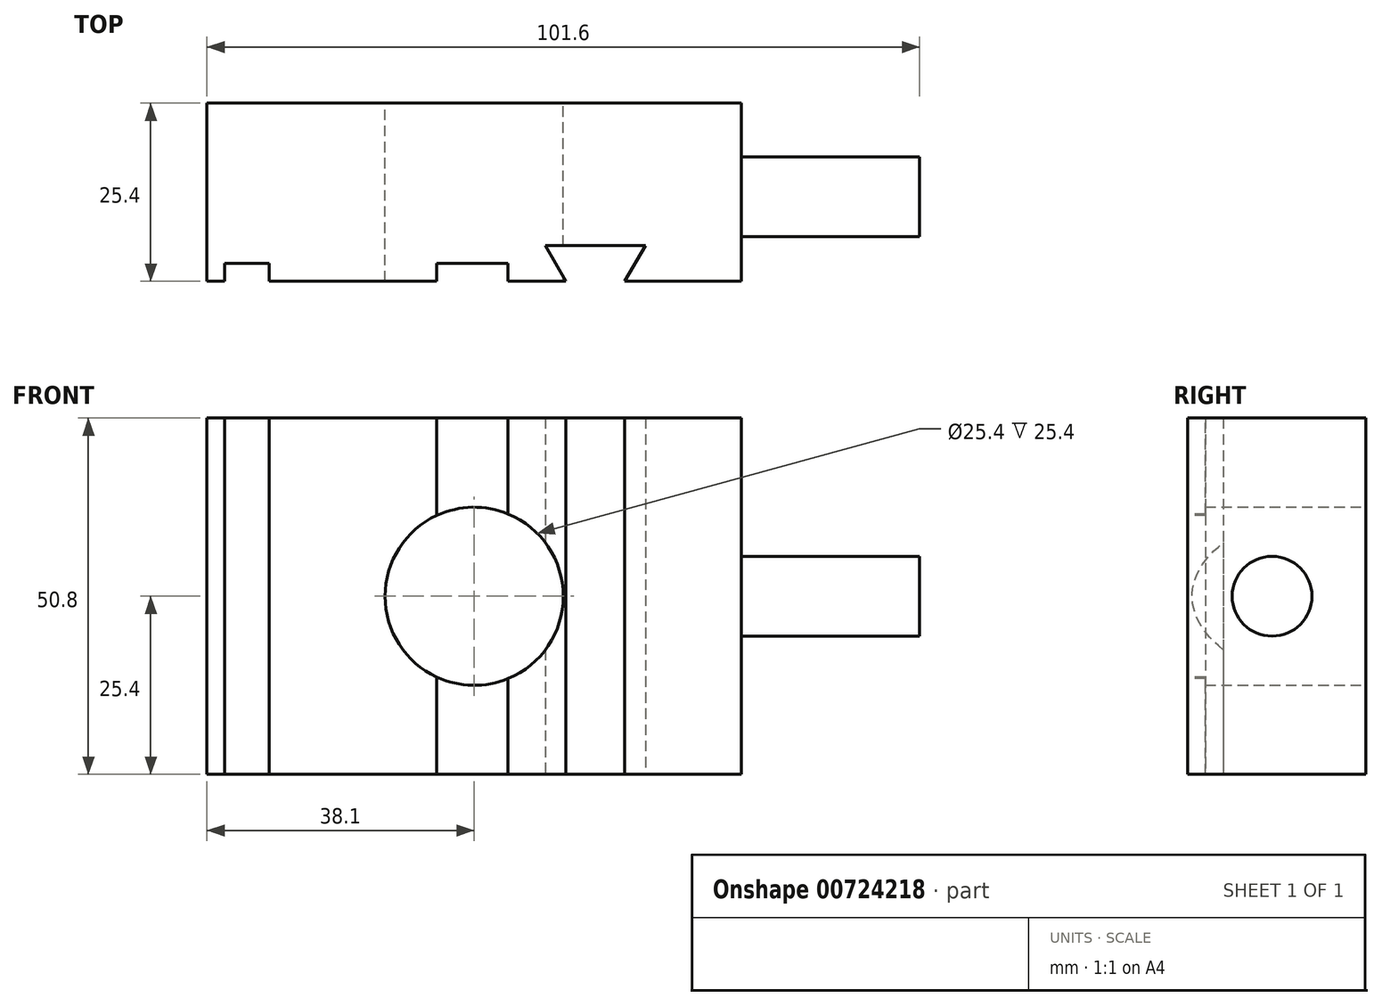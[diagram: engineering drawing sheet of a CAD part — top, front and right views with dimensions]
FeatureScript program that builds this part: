
annotation { "Feature Type Name" : "Feature", "Feature Type Description" : "" }
export const myFeature = defineFeature(function(context is Context, id is Id, definition is map)
    precondition{}
    {
        {
            var Q0;
            Q0=qCreatedBy(makeId("Front.planeOp"),FACE);
            var sketch = newSketch(context, id + "F0", { "sketchPlane" : qUnion([Q0])});
            skLineSegment(sketch, "E0.bottom", {"start": v(38.1, 25.4) * mm, "end": v(-38.1, 25.4) * mm});
            skLineSegment(sketch, "E0.top", {"start": v(38.1, -25.4) * mm, "end": v(-38.1, -25.4) * mm});
            skLineSegment(sketch, "E0.left", {"start": v(38.1, 25.4) * mm, "end": v(38.1, -25.4) * mm});
            skLineSegment(sketch, "E0.right", {"start": v(-38.1, 25.4) * mm, "end": v(-38.1, -25.4) * mm});
            skPoint(sketch, "E0.middle", {"position": v(0, 0) * mm});
            skCircle(sketch, "E1", {"center": v(0, 0) * mm, "radius": 12.7 * mm});
            skSolve(sketch);
        }
        {
            var Q0;
            Q0=makeQuery(id+"F0.imprint","IMPRINT",FACE,{"disambiguationData":[TD([[makeQuery(id+"F0.imprint","IMPRINT",EDGE,{"derivedFrom":sQuery(id+"F0.wireOp",EDGE,"E0.bottom")}),1.0]])]});
            extrude(context, id + "F1", {"entities" : qUnion([Q0]), "depth" : 25.4 * mm, "offsetDistance" : 25.4 * mm});
        }
        {
            var Q0;
            Q0=makeQuery(id+"F1.opExtrude","CAP_FACE",FACE,{"disambiguationData":[OSD([sQuery(id+"F0.wireOp",EDGE,"E0.bottom"),sQuery(id+"F0.wireOp",EDGE,"E0.top"),sQuery(id+"F0.wireOp",EDGE,"E0.left"),sQuery(id+"F0.wireOp",EDGE,"E0.right"),sQuery(id+"F0.wireOp",EDGE,"E1")])],"isStart":false});
            var sketch = newSketch(context, id + "F2", { "sketchPlane" : qUnion([Q0])});
            skLineSegment(sketch, "E2.bottom", {"start": v(-35.56, 25.4) * mm, "end": v(-29.2, 25.4) * mm});
            skLineSegment(sketch, "E2.top", {"start": v(-35.56, -25.4) * mm, "end": v(-29.2, -25.4) * mm});
            skLineSegment(sketch, "E2.left", {"start": v(-35.56, 25.4) * mm, "end": v(-35.56, -25.4) * mm});
            skLineSegment(sketch, "E2.right", {"start": v(-29.2, 25.4) * mm, "end": v(-29.2, -25.4) * mm});
            skLineSegment(sketch, "E3", {"start": v(-5.32, 25.4) * mm, "end": v(-5.32, -25.4) * mm});
            skLineSegment(sketch, "E4", {"start": v(-5.32, -25.4) * mm, "end": v(4.84, -25.4) * mm});
            skLineSegment(sketch, "E5", {"start": v(4.84, -25.4) * mm, "end": v(4.84, 25.4) * mm});
            skLineSegment(sketch, "E6", {"start": v(4.84, 25.4) * mm, "end": v(-5.32, 25.4) * mm});
            skPoint(sketch, "E7", {"position": v(0, 0) * mm});
            skLineSegment(sketch, "E8", {"start": v(-0.24, 25.4) * mm, "end": v(0, -25.4) * mm, "construction": true});
            skSolve(sketch);
        }
        {
            var Q0;
            Q0=makeQuery(id+"F2.imprint","IMPRINT",FACE,{"disambiguationData":[TD([[makeQuery(id+"F2.imprint","IMPRINT",EDGE,{"derivedFrom":sQuery(id+"F2.wireOp",EDGE,"E2.bottom")}),1.0]])]});
            var Q1;
            {var subQ0=sQuery(id+"F2.wireOp",EDGE,"E4");Q1=makeQuery(id+"F2.imprint","IMPRINT",FACE,{"disambiguationData":[TD([[makeQuery(id+"F2.imprint","IMPRINT",EDGE,{"derivedFrom":subQ0}),-1.0]])]});}
            var Q2;
            {var subQ0=sQuery(id+"F2.wireOp",EDGE,"E6");Q2=makeQuery(id+"F2.imprint","IMPRINT",FACE,{"disambiguationData":[TD([[makeQuery(id+"F2.imprint","IMPRINT",EDGE,{"derivedFrom":subQ0}),1.0]])]});}
            extrude(context, id + "F3", {"entities" : qUnion([Q0, Q1, Q2]), "operationType" : NewBodyOperationType.REMOVE, "oppositeDirection" : true, "depth" : 2.54 * mm, "offsetDistance" : 25.4 * mm});
        }
        {
            var Q0;
            Q0=makeQuery(id+"F1.opExtrude","SWEPT_FACE",FACE,{"disambiguationData":[OSD([sQuery(id+"F0.wireOp",EDGE,"E0.top")])]});
            var sketch = newSketch(context, id + "F4", { "sketchPlane" : qUnion([Q0])});
            skLineSegment(sketch, "E9", {"start": v(13.09, 25.4) * mm, "end": v(10.15, 20.32) * mm});
            skLineSegment(sketch, "E10", {"start": v(10.15, 20.32) * mm, "end": v(24.4, 20.32) * mm});
            skLineSegment(sketch, "E11", {"start": v(24.4, 20.32) * mm, "end": v(21.47, 25.4) * mm});
            skLineSegment(sketch, "E12", {"start": v(21.47, 25.4) * mm, "end": v(21.47, 25.4) * mm});
            skLineSegment(sketch, "E13", {"start": v(21.47, 25.4) * mm, "end": v(13.09, 25.4) * mm});
            skSolve(sketch);
        }
        {
            var Q0;
            Q0=makeQuery(id+"F4.imprint","IMPRINT",FACE,{"disambiguationData":[TD([[makeQuery(id+"F4.imprint","IMPRINT",EDGE,{"derivedFrom":sQuery(id+"F4.wireOp",EDGE,"E9")}),1.0]])]});
            extrude(context, id + "F5", {"entities" : qUnion([Q0]), "operationType" : NewBodyOperationType.REMOVE, "endBound" : BoundingType.THROUGH_ALL, "oppositeDirection" : true, "depth" : 25.4 * mm, "offsetDistance" : 25.4 * mm});
        }
        {
            var Q0;
            Q0=makeQuery(id+"F1.opExtrude","SWEPT_FACE",FACE,{"disambiguationData":[OSD([sQuery(id+"F0.wireOp",EDGE,"E0.left")])]});
            var sketch = newSketch(context, id + "F6", { "sketchPlane" : qUnion([Q0])});
            skCircle(sketch, "E14", {"center": v(-13.34, 0) * mm, "radius": 5.68 * mm});
            skSolve(sketch);
        }
        {
            var Q0;
            Q0 = qSketchRegion(id + "F6", true);
            extrude(context, id + "F7", {"entities" : qUnion([Q0]), "operationType" : NewBodyOperationType.ADD, "depth" : 25.4 * mm, "offsetDistance" : 25.4 * mm});
        }
    });
